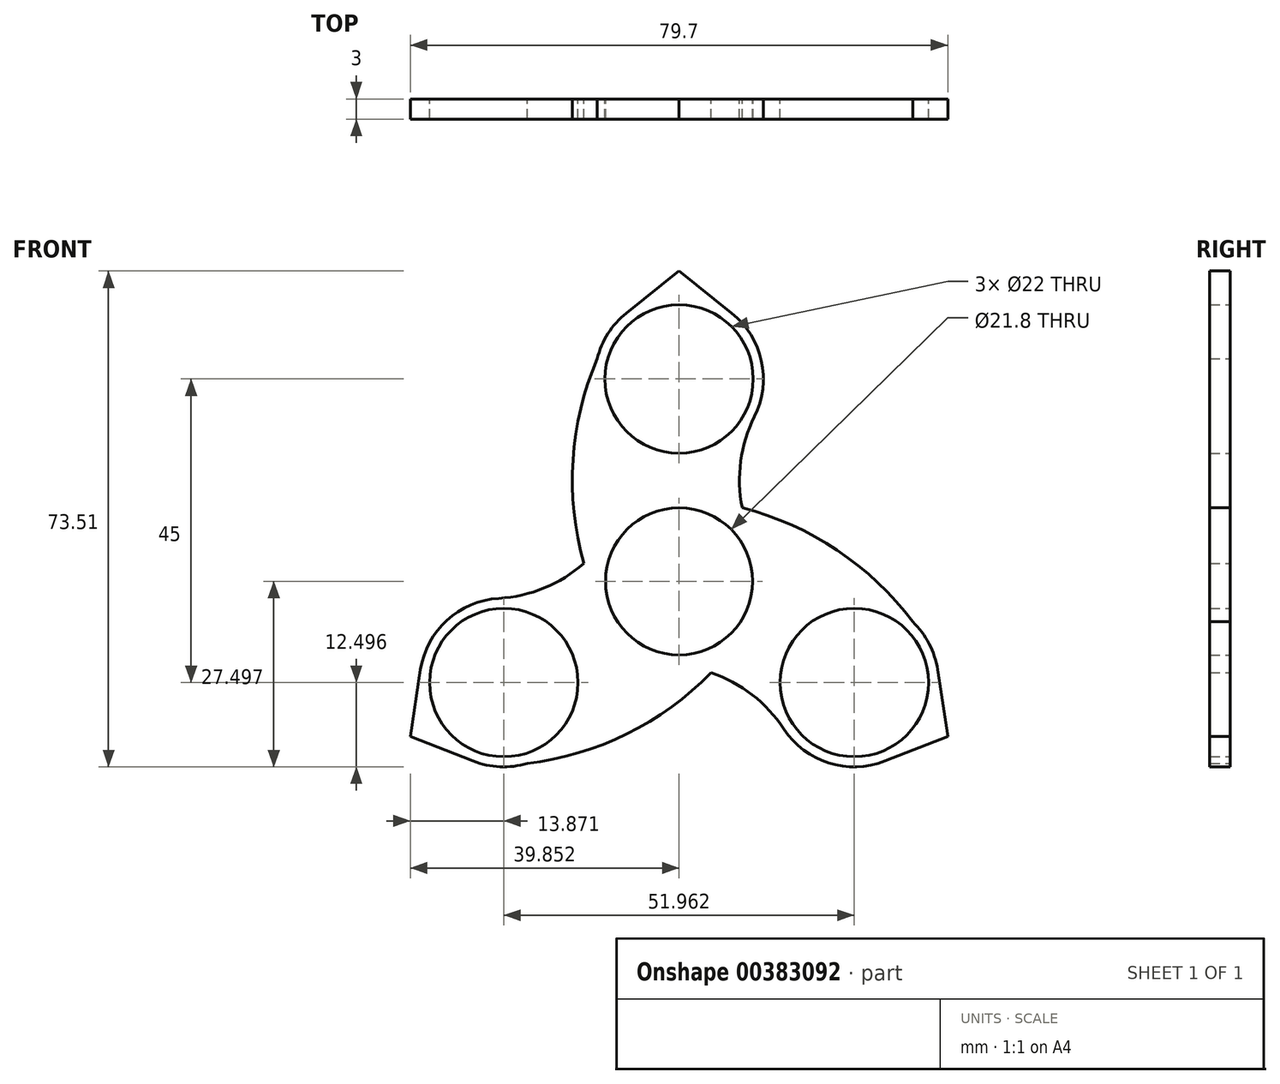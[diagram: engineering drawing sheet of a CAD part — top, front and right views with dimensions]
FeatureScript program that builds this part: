
annotation { "Feature Type Name" : "Feature", "Feature Type Description" : "" }
export const myFeature = defineFeature(function(context is Context, id is Id, definition is map)
    precondition{}
    {
        {
            var Q0;
            Q0=qCreatedBy(makeId("Front.planeOp"),FACE);
            var sketch = newSketch(context, id + "F0", { "sketchPlane" : qUnion([Q0])});
            skCircle(sketch, "E0", {"center": v(-95.2, 28.73) * mm, "radius": 10.9 * mm});
            skCircle(sketch, "E1", {"center": v(-95.2, 58.73) * mm, "radius": 11 * mm});
            skLineSegment(sketch, "E2", {"start": v(-95.2, 4.15) * mm, "end": v(-95.2, 105.99) * mm, "construction": true});
            skPoint(sketch, "E3", {"position": v(-95.2, 43.73) * mm});
            skLineSegment(sketch, "E4", {"start": v(-65.2, 43.73) * mm, "end": v(-185.55, 95.15) * mm, "construction": true});
            skLineSegment(sketch, "E5", {"start": v(-65.2, 43.73) * mm, "end": v(-85.63, 38.68) * mm, "construction": true});
            skPoint(sketch, "E6", {"position": v(-107.33, 61.73) * mm});
            skPoint(sketch, "E7", {"position": v(-107.33, 25.72) * mm});
            skArc(sketch, "E8", {"start": v(-107.33, 61.73) * mm, "mid": v(-110.92, 46.72) * mm, "end": v(-109.32, 31.38) * mm});
            skArc(sketch, "E9", {"start": v(-84.02, 53.14) * mm, "mid": v(-86.05, 46.54) * mm, "end": v(-85.84, 39.63) * mm});
            skArc(sketch, "E10", {"start": v(-85.96, 52.75) * mm, "mid": v(-86, 52.69) * mm, "end": v(-86.02, 52.62) * mm});
            skArc(sketch, "E11.trimOffspring", {"start": v(-84.02, 53.14) * mm, "mid": v(-82.99, 61.4) * mm, "end": v(-87.39, 68.48) * mm});
            skLineSegment(sketch, "E12", {"start": v(-87.39, 68.48) * mm, "end": v(-95.2, 74.74) * mm});
            skLineSegment(sketch, "E13", {"start": v(-95.2, 74.74) * mm, "end": v(-103.01, 68.48) * mm});
            skPoint(sketch, "E14.trimOffspring.end.orphan", {"position": v(-115.2, 58.73) * mm});
            skLineSegment(sketch, "E15.1.0", {"start": v(-133.54, 15.61) * mm, "end": v(-135.05, 5.72) * mm});
            skPoint(sketch, "E15.1.1", {"position": v(-86.53, 19.72) * mm});
            skPoint(sketch, "E15.1.2", {"position": v(-117.71, 1.72) * mm});
            skPoint(sketch, "E15.1.3", {"position": v(-111.18, -3.6) * mm});
            skCircle(sketch, "E15.1.5", {"center": v(-121.18, 13.73) * mm, "radius": 11 * mm});
            skArc(sketch, "E15.1.8", {"start": v(-121.93, 26.2) * mm, "mid": v(-115.2, 27.74) * mm, "end": v(-109.32, 31.38) * mm});
            skArc(sketch, "E15.1.9", {"start": v(-121.93, 26.2) * mm, "mid": v(-129.6, 22.96) * mm, "end": v(-133.54, 15.61) * mm});
            skArc(sketch, "E15.1.10", {"start": v(-117.71, 1.72) * mm, "mid": v(-102.93, 6.11) * mm, "end": v(-90.44, 15.17) * mm});
            skLineSegment(sketch, "E15.1.13", {"start": v(-135.05, 5.72) * mm, "end": v(-125.72, 2.08) * mm});
            skPoint(sketch, "E15.1.15", {"position": v(-108.19, 21.23) * mm});
            skArc(sketch, "E15.1.17", {"start": v(-120.62, 24.71) * mm, "mid": v(-120.55, 24.72) * mm, "end": v(-120.48, 24.73) * mm});
            skLineSegment(sketch, "E15.2.0", {"start": v(-64.67, 2.08) * mm, "end": v(-55.35, 5.72) * mm});
            skPoint(sketch, "E15.2.1", {"position": v(-91.73, 40.74) * mm});
            skPoint(sketch, "E15.2.2", {"position": v(-60.55, 22.73) * mm});
            skPoint(sketch, "E15.2.3", {"position": v(-59.22, 31.05) * mm});
            skCircle(sketch, "E15.2.5", {"center": v(-69.22, 13.73) * mm, "radius": 11 * mm});
            skArc(sketch, "E15.2.8", {"start": v(-79.65, 6.84) * mm, "mid": v(-84.35, 11.9) * mm, "end": v(-90.44, 15.17) * mm});
            skArc(sketch, "E15.2.9", {"start": v(-79.65, 6.84) * mm, "mid": v(-73, 1.81) * mm, "end": v(-64.67, 2.08) * mm});
            skArc(sketch, "E15.2.10", {"start": v(-60.55, 22.73) * mm, "mid": v(-71.75, 33.34) * mm, "end": v(-85.84, 39.63) * mm});
            skLineSegment(sketch, "E15.2.13", {"start": v(-55.35, 5.72) * mm, "end": v(-56.86, 15.61) * mm});
            skPoint(sketch, "E15.2.15", {"position": v(-82.2, 21.23) * mm});
            skArc(sketch, "E15.2.17", {"start": v(-79.01, 8.72) * mm, "mid": v(-79.05, 8.77) * mm, "end": v(-79.1, 8.83) * mm});
            skLineSegment(sketch, "E16.trimOffspring", {"start": v(-89.17, 37.8) * mm, "end": v(-198.58, 10.79) * mm, "construction": true});
            skPoint(sketch, "E17.orphan", {"position": v(-87.76, 38.77) * mm});
            skPoint(sketch, "E18.orphan", {"position": v(-107.62, 30.14) * mm});
            skArc(sketch, "E19.trimOffspring", {"start": v(-56.86, 15.61) * mm, "mid": v(-58.12, 19.48) * mm, "end": v(-60.55, 22.73) * mm});
            skArc(sketch, "E20.trimOffspring", {"start": v(-125.72, 2.08) * mm, "mid": v(-121.75, 1.24) * mm, "end": v(-117.71, 1.72) * mm});
            skPoint(sketch, "E21.orphan", {"position": v(-105.63, 35.61) * mm});
            skPoint(sketch, "E22.orphan", {"position": v(-87.18, 49.13) * mm});
            skPoint(sketch, "E23.orphan", {"position": v(-84.64, 52.03) * mm});
            skPoint(sketch, "E24.orphan", {"position": v(-84.88, 54.92) * mm});
            skArc(sketch, "E25.trimOffspring", {"start": v(-103.01, 68.48) * mm, "mid": v(-105.73, 65.46) * mm, "end": v(-107.33, 61.73) * mm});
            skPoint(sketch, "E26.orphan", {"position": v(-77.67, 6.69) * mm});
            skPoint(sketch, "E27.orphan", {"position": v(-80.3, 7.93) * mm});
            skPoint(sketch, "E28.orphan", {"position": v(-123.05, 24.57) * mm});
            skPoint(sketch, "E29.orphan", {"position": v(-120.66, 26.22) * mm});
            skSolve(sketch);
        }
        {
            var Q0;
            Q0 = qSketchRegion(id + "F0", true);
            extrude(context, id + "F1", {"entities" : qUnion([Q0]), "depth" : 3 * mm, "offsetDistance" : 25 * mm});
        }
    });
